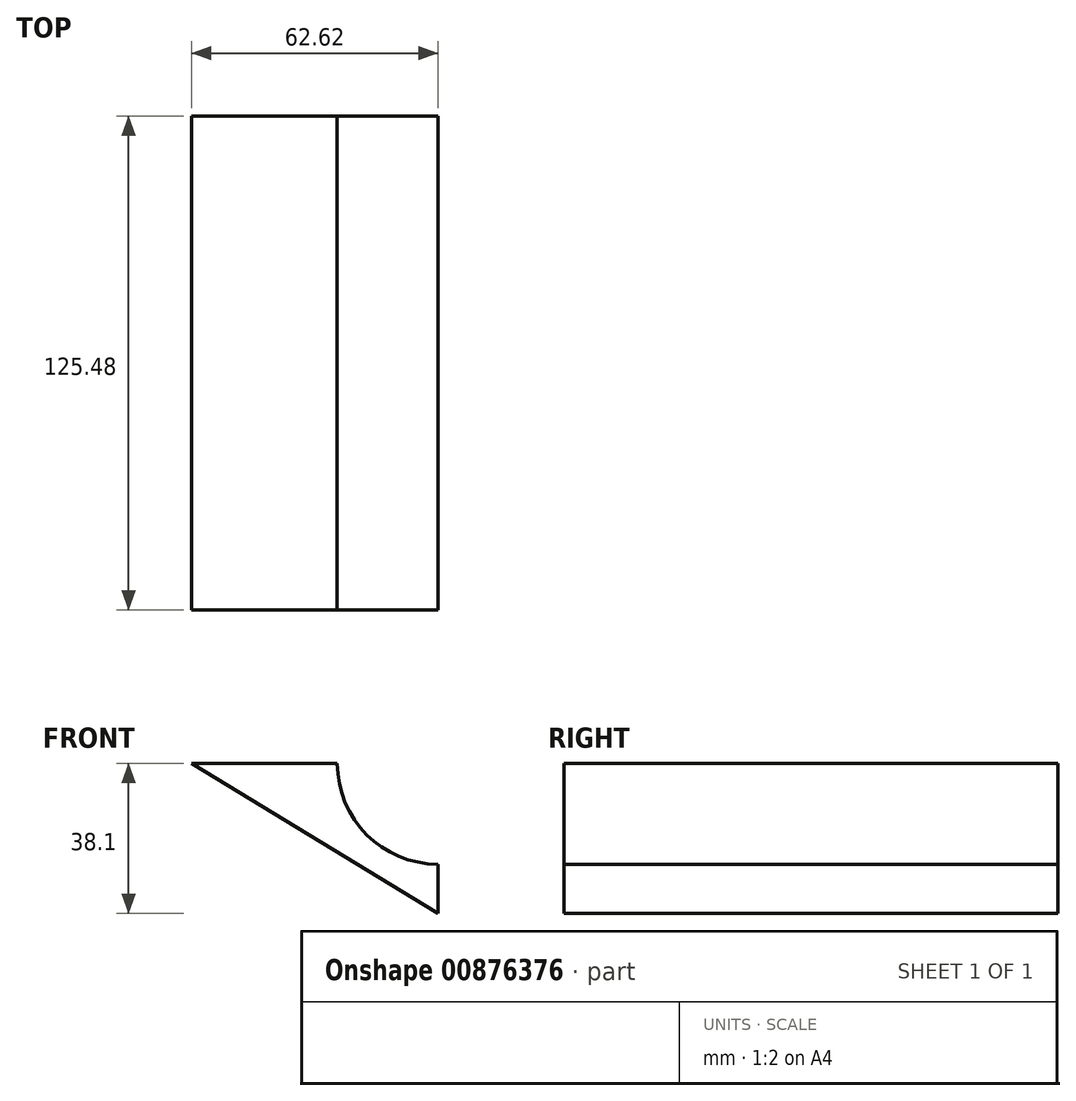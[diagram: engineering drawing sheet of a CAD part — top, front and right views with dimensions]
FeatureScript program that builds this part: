
annotation { "Feature Type Name" : "Feature", "Feature Type Description" : "" }
export const myFeature = defineFeature(function(context is Context, id is Id, definition is map)
    precondition{}
    {
        {
            var Q0;
            Q0=qCreatedBy(makeId("Front.planeOp"),FACE);
            var sketch = newSketch(context, id + "F0", { "sketchPlane" : qUnion([Q0])});
            skLineSegment(sketch, "E0", {"start": v(-41.91, 47.38) * mm, "end": v(20.7, 47.38) * mm});
            skLineSegment(sketch, "E1", {"start": v(20.7, 47.38) * mm, "end": v(20.7, 9.28) * mm});
            skLineSegment(sketch, "E2", {"start": v(20.7, 9.28) * mm, "end": v(-41.91, 47.38) * mm});
            skArc(sketch, "E3", {"start": v(-4.88, 47.38) * mm, "mid": v(2.61, 29.28) * mm, "end": v(20.7, 21.79) * mm});
            skSolve(sketch);
        }
        {
            var Q0;
            {var subQ0=sQuery(id+"F0.wireOp",EDGE,"E2");Q0=makeQuery(id+"F0.imprint","IMPRINT",FACE,{"disambiguationData":[TD([[makeQuery(id+"F0.imprint","IMPRINT",EDGE,{"derivedFrom":subQ0}),-1.0]])]});}
            extrude(context, id + "F1", {"entities" : qUnion([Q0]), "depth" : 125.48 * mm, "offsetDistance" : 25.4 * mm});
        }
    });
